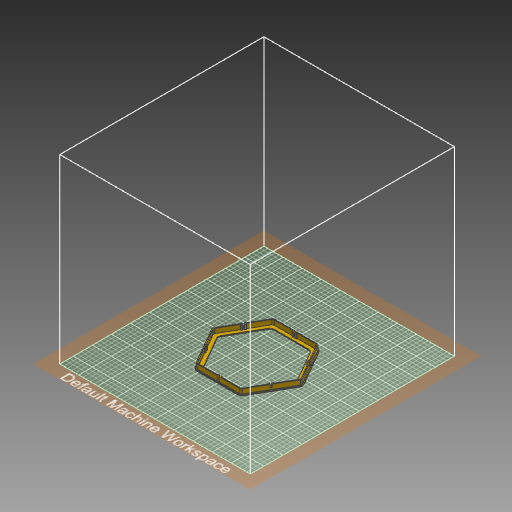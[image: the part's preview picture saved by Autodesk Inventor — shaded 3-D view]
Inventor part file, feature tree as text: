
AUTODESK INVENTOR PART (.ipt)
format: ipt  version: 2019 (Build 230136000, 136)  size: 566,272 bytes
history: native  units: mm
features: extrude x5, sketch x5, projected_geometry x3, fillet x2, other x1, pattern_circular x1
ambient origin geometry x8: Origin, YZ Plane, XZ Plane, XY Plane, X Axis, Y Axis, Z Axis, Center Point
bodies: Solid1 (feature_tree)
feature tree (17):
  extrude  "Extrusion1"  Depth=2.0mm
  extrude  "Extrusion5"  Depth=2.0mm
  extrude  "Extrusion6"  Depth=10.0mm
  fillet  "Fillet1"  [1 undecoded]
  fillet  "Fillet2"  Radius=8.0mm
  extrude  "Extrusion7"  TaperAngle=0.0deg  [1 undecoded]
  extrude  "Extrusion8"  Depth=4.0mm
  other  "Work Axis2"
  pattern_circular  "Circular Pattern1"  [2 undecoded]
  sketch  "Sketch1"  dims[d0=175.0mm d1=2.0mm]
  sketch  "Sketch5"  dims[d2=0.0mm d15=2.0mm]
  projected_geometry  "Projected Loop4"
  sketch  "Sketch7"  dims[d16=2.0mm d17=10.0mm d18=0.0mm d19=8.0mm]
  projected_geometry  "Projected Loop6"
  sketch  "Sketch8"  dims[d20=7.0mm d21=0.0mm]
  sketch  "Sketch9"  dims[d22=10.0mm d23=4.0mm d24=10.0mm d25=3.3mm d26=6.5mm d27=0.0mm d28=4.0mm d29=3.0mm d30=5.0mm d31=0.0mm d32=60.0mm d33=360.0deg]
  projected_geometry  "Projected Loop7"
note: 4 required parameter values undecoded (feature->parameter linkage not recoverable at this tier; creation-order binding heuristic only, values carry confidence <= 0.55)
